# Revit family: BVN_BRF
name_source: partatom
category: Mechanical Equipment
units: mm (PartAtom-declared; Revit-internal decimal feet)

## family parameters
Cut with Voids When Loaded = No
Host = Face
Part Type = Normal
Room Calculation Point = No
Round Connector Dimension = Use Diameter
Shared = No

## types (10) — shared parameters
Default Elevation = 1219 mm
Description = Roof Fan
Frequency = 50 Hz
Manufacturer = Bahçıvan Elektrik Motor San. ve Tic. Ltd. Şti.
Material = <By Category>
Model = BRF
Protection Class = 44
URL = http://www.bahcivanmotor.com.tr

## per-type parameters (varying)
| type | A | Air Flow | B | B' | C | Capacitor (mF) | Current | D | D-C | F | G | Insulation Class | Power | Q(Alt) | Sound Pressure Level dB(A) | Speed(d/d) | Tepe Genislik | Tepe(Cap) | Voltage | Weight | h(Tepe) | h_Koni |
| BRF 400 | 595 mm | 4600.0 m³/h | 685 mm | 520 mm | 145 mm  [stored 0.475722 ft] | 10 | 2 A | 355 mm | 210 mm | 270 mm  [stored 0.885827 ft] | 40 mm  [stored 0.131234 ft] | F | 460 W | 520 mm | 51 | 1560 | 230 mm  [stored 0.754593 ft] | 600 mm | 230 V | 22.00 kg | 65 mm  [stored 0.213255 ft] | 80 mm  [stored 0.262467 ft] |
| BRF 160 | 252 mm  [stored 0.826772 ft] | 400.0 m³/h | 260 mm  [stored 0.853018 ft] | 190 mm | 50 mm  [stored 0.164042 ft] | 2 | 0 A | 140 mm  [stored 0.459318 ft] | 90 mm  [stored 0.295276 ft] | 80 mm  [stored 0.262467 ft] | 25 mm  [stored 0.082021 ft] | B | 60 W | 200 mm  [stored 0.656168 ft] | 44 | 3000 | 80 mm  [stored 0.262467 ft] | 200 mm  [stored 0.656168 ft] | 230 V | 3.50 kg | 20 mm | 30 mm  [stored 0.0984252 ft] |
| BRF 180 | 252 mm  [stored 0.826772 ft] | 500.0 m³/h | 260 mm  [stored 0.853018 ft] | 190 mm | 50 mm  [stored 0.164042 ft] | 2.5 | 0 A | 140 mm  [stored 0.459318 ft] | 90 mm  [stored 0.295276 ft] | 80 mm  [stored 0.262467 ft] | 25 mm  [stored 0.082021 ft] | B | 90 W | 200 mm  [stored 0.656168 ft] | 49 | 2750 | 80 mm  [stored 0.262467 ft] | 200 mm  [stored 0.656168 ft] | 230 V | 3.70 kg | 20 mm | 30 mm  [stored 0.0984252 ft] |
| BRF 225 | 336 mm | 1020.0 m³/h | 386 mm | 300 mm | 105 mm  [stored 0.344488 ft] | 3 | 1 A | 212 mm  [stored 0.695538 ft] | 107 mm | 146 mm  [stored 0.479003 ft] | 35 mm  [stored 0.114829 ft] | B | 100 W | 280 mm | 50 | 3100 | 140 mm  [stored 0.459318 ft] | 500 mm | 230 V | 7.00 kg | 45 mm | 60 mm  [stored 0.19685 ft] |
| BRF 250 | 370 mm | 1375.0 m³/h | 386 mm | 300 mm | 105 mm  [stored 0.344488 ft] | 6 | 1 A | 225 mm  [stored 0.738189 ft] | 120 mm | 163 mm  [stored 0.534777 ft] | 35 mm  [stored 0.114829 ft] | B | 175 W | 300 mm | 52 | 3180 | 140 mm  [stored 0.459318 ft] | 500 mm | 230 V | 8.00 kg | 40 mm  [stored 0.131234 ft] | 65 mm  [stored 0.213255 ft] |
| BRF 315 | 454 mm | 2315.0 m³/h | 443 mm | 350 mm | 135 mm  [stored 0.442913 ft] | 3 | 1 A | 293 mm | 158 mm | 185 mm  [stored 0.606955 ft] | 40 mm  [stored 0.131234 ft] | F | 155 W | 350 mm | 47 | 1650 | 160 mm  [stored 0.524934 ft] | 600 mm | 230 V | 12.80 kg | 50 mm  [stored 0.164042 ft] | 85 mm  [stored 0.278871 ft] |
| BRF 355 | 595 mm | 3500.0 m³/h | 595 mm | 450 mm | 135 mm  [stored 0.442913 ft] | 6 | 1 A | 285 mm | 150 mm | 234 mm  [stored 0.767717 ft] | 40 mm  [stored 0.131234 ft] | F | 245 W | 450 mm | 46 | 1680 | 200 mm  [stored 0.656168 ft] | 600 mm | 230 V | 18.00 kg | 65 mm  [stored 0.213255 ft] | 70 mm  [stored 0.229659 ft] |
| BRF 450 | 664 mm | 6000.0 m³/h | 685 mm | 560 mm | 145 mm  [stored 0.475722 ft] | 10 | 3 A | 400 mm | 255 mm | 282 mm | 40 mm  [stored 0.131234 ft] | F | 655 W | 560 mm | 52 | 1525 | 250 mm  [stored 0.82021 ft] | 600 mm | 230 V | 28.00 kg | 65 mm  [stored 0.213255 ft] | 80 mm  [stored 0.262467 ft] |
| BRF 500 | 798 mm | 7600.0 m³/h | 824 mm | 720 mm | 155 mm  [stored 0.50853 ft] | 0 | 2 A | 385 mm | 230 mm  [stored 0.754593 ft] | 320 mm | 40 mm  [stored 0.131234 ft] | F | 840 W | 720 mm | 54 | 1360 | 320 mm | 600 mm | 380 V | 45.50 kg | 75 mm | 80 mm  [stored 0.262467 ft] |
| BRF 560 | 798 mm | 9800.0 m³/h | 824 mm | 720 mm | 155 mm  [stored 0.50853 ft] | 0 | 3 A | 400 mm | 245 mm | 320 mm | 40 mm  [stored 0.131234 ft] | F | 1440 W | 720 mm | 66 | 1300 | 320 mm | 600 mm | 380 V | 48.00 kg | 75 mm | 80 mm  [stored 0.262467 ft] |

note: [stored X ft] marks values corroborated as IEEE doubles in the binary element streams (Revit-internal decimal feet)

## geometry (parser evidence)
native form markers: Sweep x2
no freeform markers — native parametric forms only
